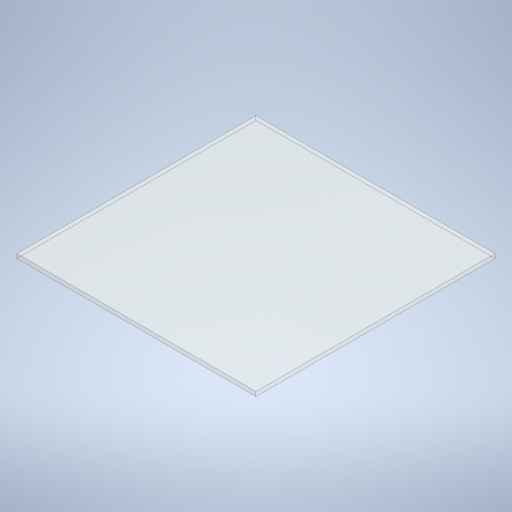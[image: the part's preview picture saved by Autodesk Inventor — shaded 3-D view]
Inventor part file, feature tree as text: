
AUTODESK INVENTOR PART (.ipt)
format: ipt  version: 2024 (Build 280153000, 153)  size: 220,160 bytes
history: native  units: in
note: dims shown in document units (in); Inventor stores cm internally (conversion verified against a paired STEP export)
features: extrude x1, sketch x1
ambient origin geometry x8: Origin, YZ Plane, XZ Plane, XY Plane, X Axis, Y Axis, Z Axis, Center Point
bodies: Solid1 (feature_tree)
feature tree (2):
  extrude  "Extrusion1"  Depth=14.0in
  sketch  "Sketch1"  dims[d0=14.0in d1=14.0in d2=0.25in d3=0.0in]
